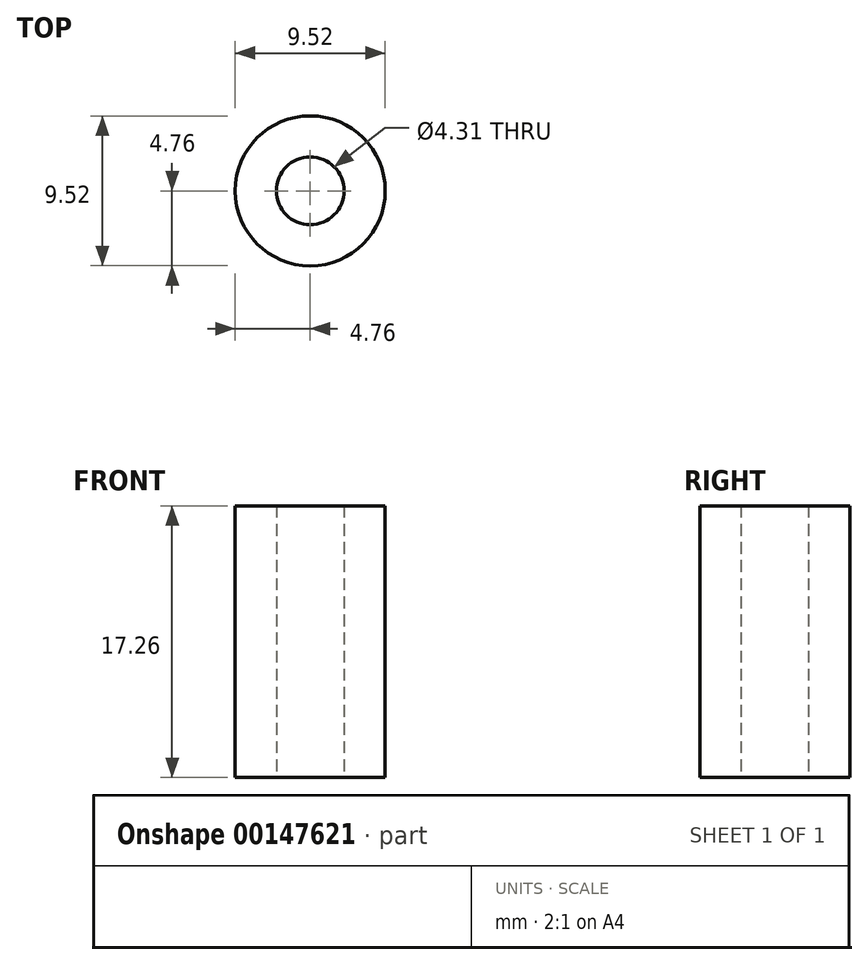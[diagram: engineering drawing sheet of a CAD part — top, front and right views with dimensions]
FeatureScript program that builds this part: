
annotation { "Feature Type Name" : "Feature", "Feature Type Description" : "" }
export const myFeature = defineFeature(function(context is Context, id is Id, definition is map)
    precondition{}
    {
        {
            var Q0;
            Q0=qCreatedBy(makeId("Top.planeOp"),FACE);
            var sketch = newSketch(context, id + "F0", { "sketchPlane" : qUnion([Q0])});
            skCircle(sketch, "E0", {"center": v(0, 0) * mm, "radius": 4.76 * mm});
            skCircle(sketch, "E1", {"center": v(0, 0) * mm, "radius": 2.15 * mm});
            skSolve(sketch);
        }
        {
            var Q0;
            Q0=qSketchRegion(id+"F0",true);
            extrude(context, id + "F1", {"entities" : qUnion([Q0]), "depth" : 17.26 * mm});
        }
    });
